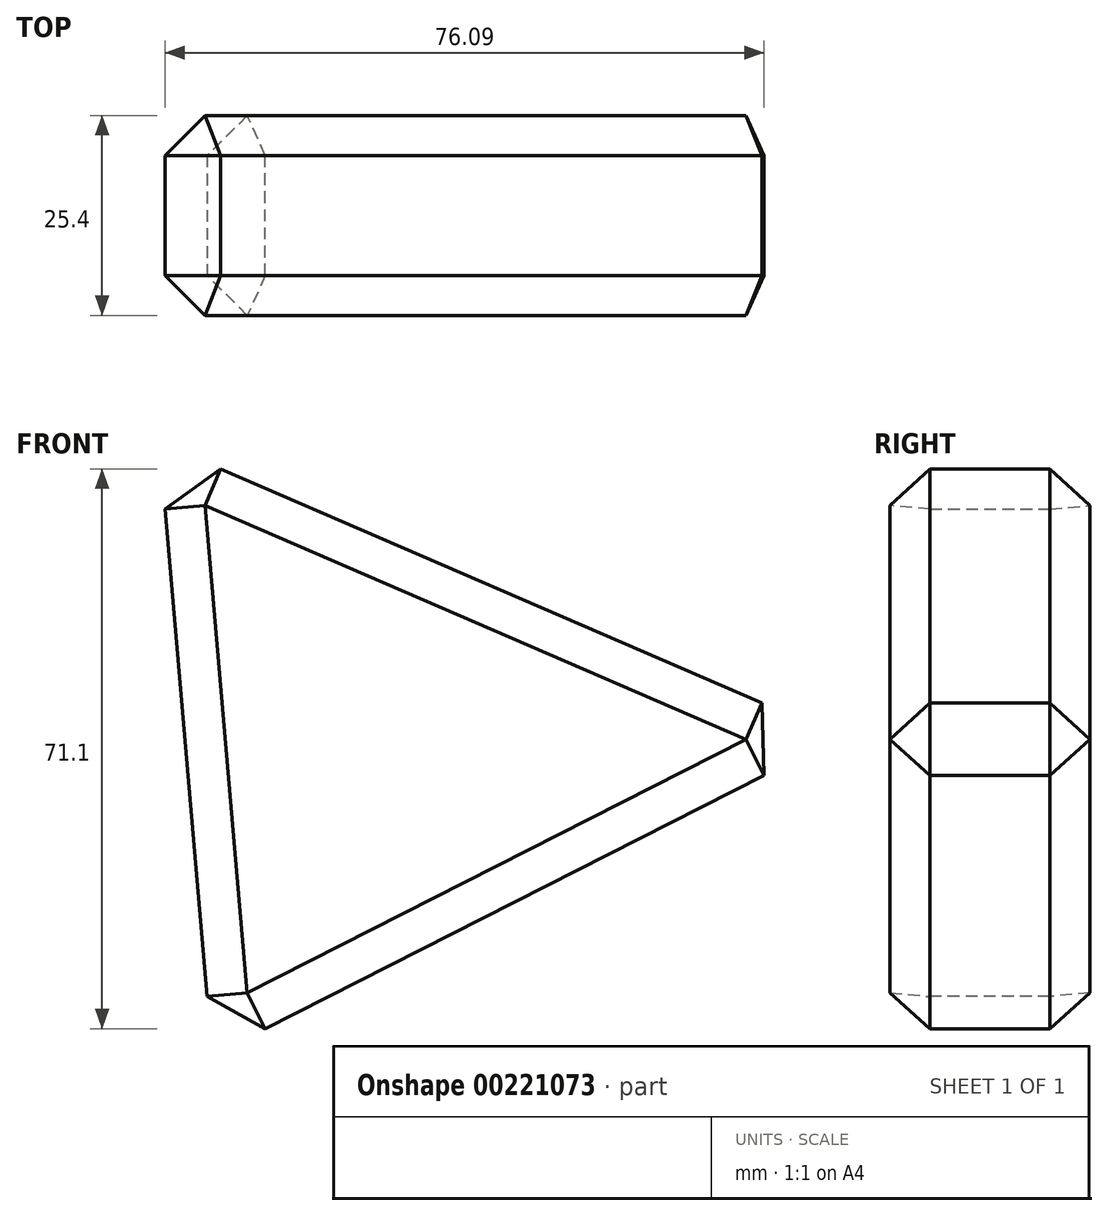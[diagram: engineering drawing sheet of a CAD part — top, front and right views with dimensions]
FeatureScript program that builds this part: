
annotation { "Feature Type Name" : "Feature", "Feature Type Description" : "" }
export const myFeature = defineFeature(function(context is Context, id is Id, definition is map)
    precondition{}
    {
        {
            var Q0;
            Q0=qCreatedBy(makeId("Front.planeOp"),FACE);
            var sketch = newSketch(context, id + "F0", { "sketchPlane" : qUnion([Q0])});
            skLineSegment(sketch, "E0", {"start": v(-41.3, 46.6) * mm, "end": v(-34.54, -31.3) * mm});
            skLineSegment(sketch, "E1", {"start": v(45.17, 9.21) * mm, "end": v(-41.3, 46.6) * mm});
            skLineSegment(sketch, "E2", {"start": v(-34.54, -31.3) * mm, "end": v(45.17, 9.21) * mm});
            skSolve(sketch);
        }
        {
            var Q0;
            Q0 = qSketchRegion(id + "F0", true);
            extrude(context, id + "F1", {"entities" : qUnion([Q0]), "depth" : 25.4 * mm});
        }
        {
            var Q0;
            Q0=makeQuery(id+"F1.opExtrude","SWEPT_FACE",FACE,{"disambiguationData":[OSD([sQuery(id+"F0.wireOp",EDGE,"E1")])]});
            var Q1;
            Q1=makeQuery(id+"F1.opExtrude","CAP_EDGE",EDGE,{"disambiguationData":[OSD([sQuery(id+"F0.wireOp",EDGE,"E0")])],"isStart":false});
            var Q2;
            Q2=makeQuery(id+"F1.opExtrude","CAP_EDGE",EDGE,{"disambiguationData":[OSD([sQuery(id+"F0.wireOp",EDGE,"E2")])],"isStart":false});
            var Q3;
            Q3=makeQuery(id+"F1.opExtrude","CAP_EDGE",EDGE,{"disambiguationData":[OSD([sQuery(id+"F0.wireOp",EDGE,"E0")])],"isStart":true});
            var Q4;
            Q4=makeQuery(id+"F1.opExtrude","SWEPT_EDGE",EDGE,{"disambiguationData":[OSD([sQuery(id+"F0.wireOp",EDGE,"E0"),sQuery(id+"F0.wireOp",EDGE,"E2")])]});
            var Q5;
            Q5=makeQuery(id+"F1.opExtrude","CAP_EDGE",EDGE,{"disambiguationData":[OSD([sQuery(id+"F0.wireOp",EDGE,"E2")])],"isStart":true});
            chamfer(context, id + "F2", {"entities" : qUnion([Q0, Q1, Q2, Q3, Q4, Q5]), "width" : 5.08 * mm, "tangentPropagation" : true});
        }
    });
